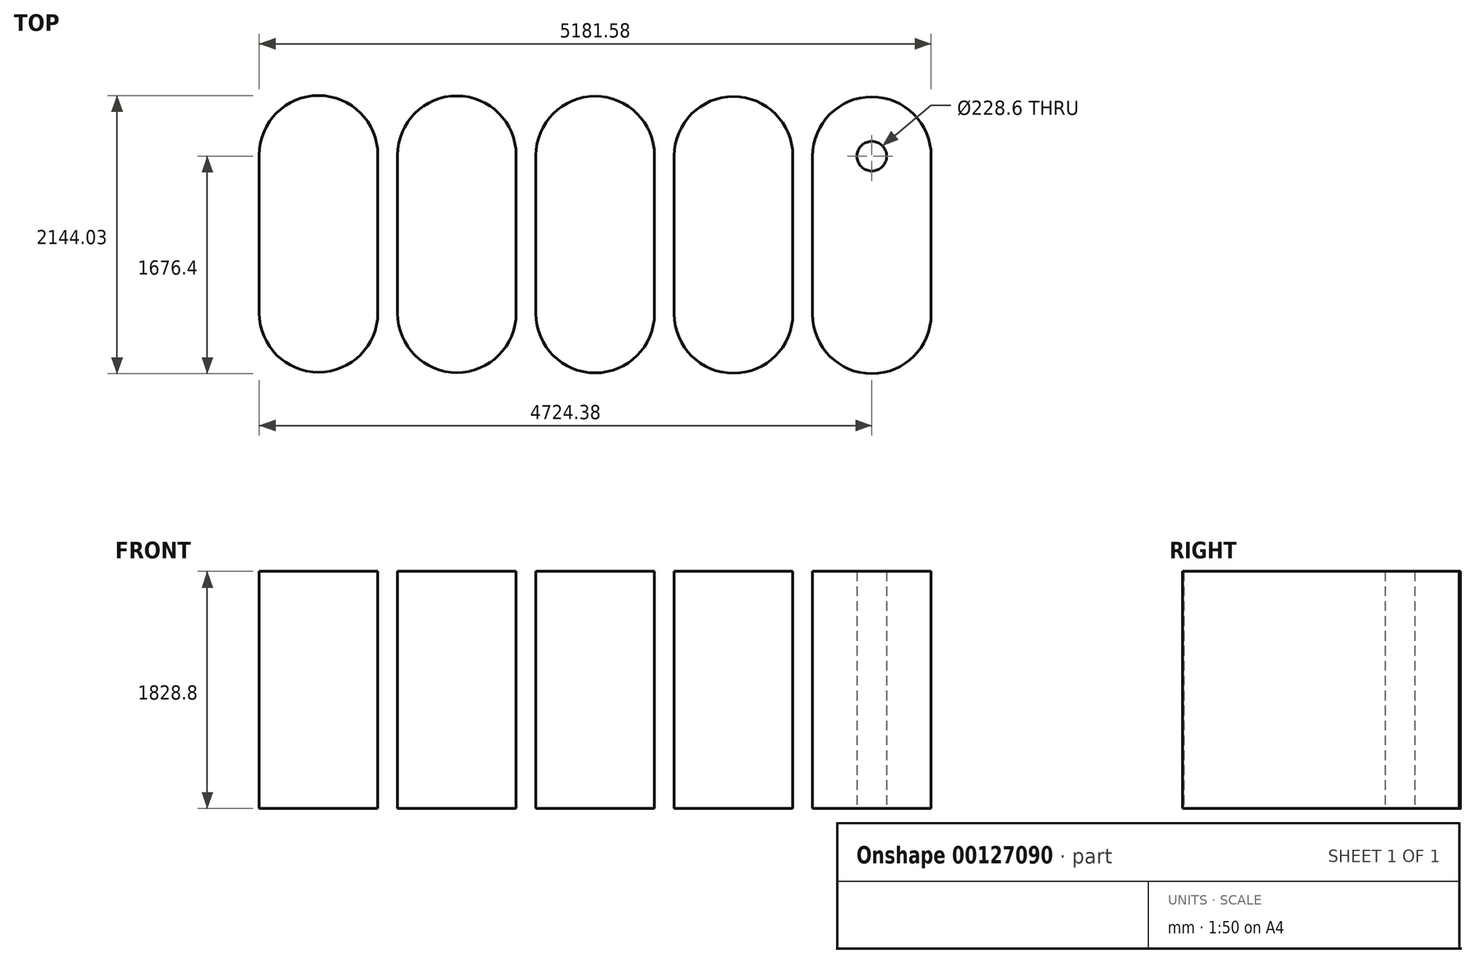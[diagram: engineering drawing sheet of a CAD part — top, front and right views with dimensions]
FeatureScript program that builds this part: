
annotation { "Feature Type Name" : "Feature", "Feature Type Description" : "" }
export const myFeature = defineFeature(function(context is Context, id is Id, definition is map)
    precondition{}
    {
        {
            var Q0;
            Q0=qCreatedBy(makeId("Top.planeOp"),FACE);
            var sketch = newSketch(context, id + "F0", { "sketchPlane" : qUnion([Q0])});
            skArc(sketch, "E0.0.startCap", {"start": v(-457.2, 1219.2) * mm, "mid": v(0, 1676.4) * mm, "end": v(457.2, 1219.2) * mm});
            skArc(sketch, "E0.0.endCap", {"start": v(457.2, 0) * mm, "mid": v(0, -457.2) * mm, "end": v(-457.2, 0) * mm});
            skLineSegment(sketch, "E0.0.left", {"start": v(457.2, 1219.2) * mm, "end": v(457.2, 0) * mm});
            skLineSegment(sketch, "E0.0.right", {"start": v(-457.2, 1219.2) * mm, "end": v(-457.2, 0) * mm});
            skLineSegment(sketch, "E1.1.0.0", {"start": v(1524, 1216.6) * mm, "end": v(1524, -2.6) * mm});
            skLineSegment(sketch, "E1.1.0.1", {"start": v(609.6, 1216.6) * mm, "end": v(609.6, -2.6) * mm});
            skArc(sketch, "E1.1.0.2", {"start": v(1524, -2.6) * mm, "mid": v(1066.8, -459.8) * mm, "end": v(609.6, -2.6) * mm});
            skArc(sketch, "E1.1.0.3", {"start": v(609.6, 1216.6) * mm, "mid": v(1066.8, 1673.8) * mm, "end": v(1524, 1216.6) * mm});
            skLineSegment(sketch, "E1.2.0.0", {"start": v(2590.8, 1213.98) * mm, "end": v(2590.8, -5.22) * mm});
            skLineSegment(sketch, "E1.2.0.1", {"start": v(1676.4, 1213.98) * mm, "end": v(1676.4, -5.22) * mm});
            skArc(sketch, "E1.2.0.2", {"start": v(2590.8, -5.22) * mm, "mid": v(2133.6, -462.42) * mm, "end": v(1676.4, -5.22) * mm});
            skArc(sketch, "E1.2.0.3", {"start": v(1676.4, 1213.98) * mm, "mid": v(2133.6, 1671.18) * mm, "end": v(2590.8, 1213.98) * mm});
            skLineSegment(sketch, "E1.direction1", {"start": v(457.2, 0) * mm, "end": v(1524, -2.6) * mm, "construction": true});
            skLineSegment(sketch, "E2.0.3.0", {"start": v(3657.6, 1211.37) * mm, "end": v(3657.6, -7.83) * mm});
            skLineSegment(sketch, "E2.3.3.0", {"start": v(2743.2, 1211.37) * mm, "end": v(2743.2, -7.83) * mm});
            skArc(sketch, "E2.6.3.0", {"start": v(3657.6, -7.83) * mm, "mid": v(3200.4, -465.03) * mm, "end": v(2743.2, -7.83) * mm});
            skArc(sketch, "E2.10.3.0", {"start": v(2743.2, 1211.37) * mm, "mid": v(3200.4, 1668.57) * mm, "end": v(3657.6, 1211.37) * mm});
            skLineSegment(sketch, "E2.0.4.0", {"start": v(4724.39, 1208.77) * mm, "end": v(4724.39, -10.43) * mm});
            skLineSegment(sketch, "E2.3.4.0", {"start": v(3809.99, 1208.77) * mm, "end": v(3809.99, -10.43) * mm});
            skArc(sketch, "E2.6.4.0", {"start": v(4724.39, -10.43) * mm, "mid": v(4267.19, -467.63) * mm, "end": v(3809.99, -10.43) * mm});
            skArc(sketch, "E2.10.4.0", {"start": v(3809.99, 1208.77) * mm, "mid": v(4267.19, 1665.97) * mm, "end": v(4724.39, 1208.77) * mm});
            skLineSegment(sketch, "E2.0.5.0", {"start": v(5791.18, 1206.16) * mm, "end": v(5791.18, -13.04) * mm});
            skLineSegment(sketch, "E2.3.5.0", {"start": v(4876.78, 1206.16) * mm, "end": v(4876.78, -13.04) * mm});
            skArc(sketch, "E2.6.5.0", {"start": v(5791.18, -13.04) * mm, "mid": v(5333.98, -470.24) * mm, "end": v(4876.78, -13.04) * mm});
            skArc(sketch, "E2.10.5.0", {"start": v(4876.78, 1206.16) * mm, "mid": v(5333.98, 1663.36) * mm, "end": v(5791.18, 1206.16) * mm});
            skCircle(sketch, "E3", {"center": v(0, 1219.2) * mm, "radius": 114.3 * mm});
            skCircle(sketch, "E4", {"center": v(5333.98, 1206.16) * mm, "radius": 114.3 * mm});
            skSolve(sketch);
        }
        {
            var Q0;
            Q0=makeQuery(id+"F0.imprint","IMPRINT",FACE,{"disambiguationData":[TD([[makeQuery(id+"F0.imprint","IMPRINT",EDGE,{"derivedFrom":sQuery(id+"F0.wireOp",EDGE,"E0.0.startCap")}),-1.0]])]});
            var Q1;
            Q1=makeQuery(id+"F0.imprint","IMPRINT",FACE,{"disambiguationData":[TD([[makeQuery(id+"F0.imprint","IMPRINT",EDGE,{"derivedFrom":sQuery(id+"F0.wireOp",EDGE,"E1.1.0.0")}),-1.0]])]});
            var Q2;
            Q2=makeQuery(id+"F0.imprint","IMPRINT",FACE,{"disambiguationData":[TD([[makeQuery(id+"F0.imprint","IMPRINT",EDGE,{"derivedFrom":sQuery(id+"F0.wireOp",EDGE,"E1.2.0.0")}),-1.0]])]});
            var Q3;
            Q3=makeQuery(id+"F0.imprint","IMPRINT",FACE,{"disambiguationData":[TD([[makeQuery(id+"F0.imprint","IMPRINT",EDGE,{"derivedFrom":sQuery(id+"F0.wireOp",EDGE,"E2.0.3.0")}),-1.0]])]});
            var Q4;
            Q4=makeQuery(id+"F0.imprint","IMPRINT",FACE,{"disambiguationData":[TD([[makeQuery(id+"F0.imprint","IMPRINT",EDGE,{"derivedFrom":sQuery(id+"F0.wireOp",EDGE,"E2.0.4.0")}),-1.0]])]});
            var Q5;
            Q5=makeQuery(id+"F0.imprint","IMPRINT",FACE,{"disambiguationData":[TD([[makeQuery(id+"F0.imprint","IMPRINT",EDGE,{"derivedFrom":sQuery(id+"F0.wireOp",EDGE,"E2.0.5.0")}),-1.0]])]});
            extrude(context, id + "F1", {"entities" : qUnion([Q0, Q1, Q2, Q3, Q4, Q5]), "depth" : 1828.8 * mm});
        }
    });
